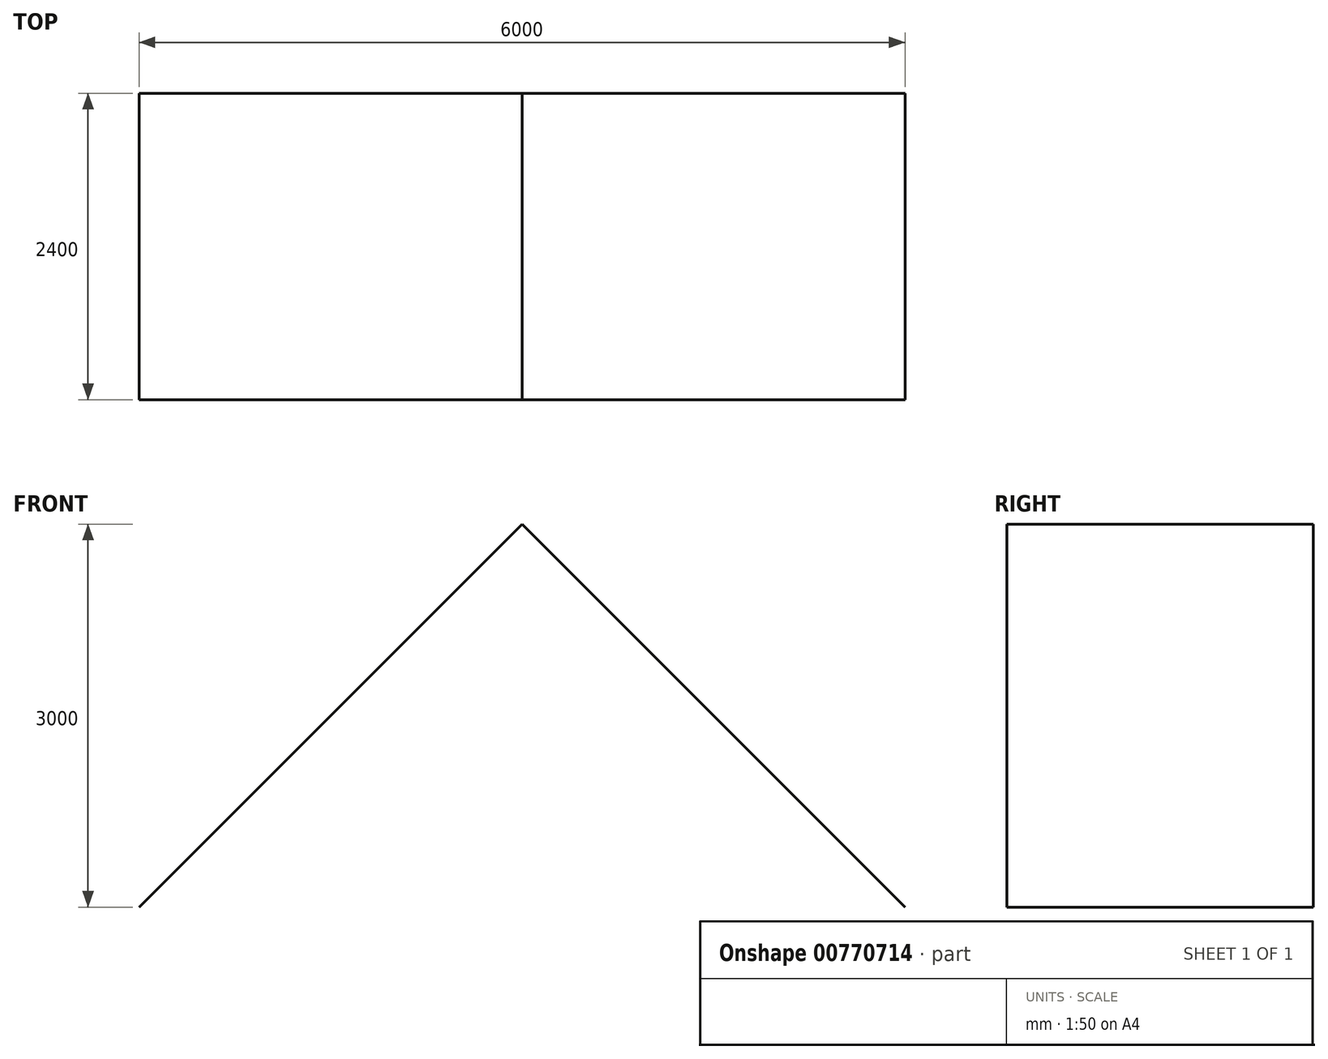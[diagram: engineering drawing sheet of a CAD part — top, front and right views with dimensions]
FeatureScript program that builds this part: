
annotation { "Feature Type Name" : "Feature", "Feature Type Description" : "" }
export const myFeature = defineFeature(function(context is Context, id is Id, definition is map)
    precondition{}
    {
        {
            var Q0;
            Q0=qCreatedBy(makeId("Front.planeOp"),FACE);
            var sketch = newSketch(context, id + "F0", { "sketchPlane" : qUnion([Q0])});
            skLineSegment(sketch, "E0", {"start": v(-3000, 0) * mm, "end": v(0, 3000) * mm});
            skLineSegment(sketch, "E1.MirrorCS", {"start": v(3000, 0) * mm, "end": v(0, 3000) * mm});
            skLineSegment(sketch, "E2", {"start": v(-3000, 0) * mm, "end": v(0, 0) * mm, "construction": true});
            skSolve(sketch);
        }
        {
            var Q0;
            Q0 = qSketchRegion(id + "F0", true);
            var Q1;
            Q1=sQuery(id+"F0.wireOp",EDGE,"E0");
            var Q2;
            Q2=sQuery(id+"F0.wireOp",EDGE,"E1.MirrorCS");
            extrude(context, id + "F1", {"entities" : qUnion([Q0]), "bodyType" : ToolBodyType.SURFACE, "surfaceEntities" : qUnion([Q1, Q2]), "depth" : 2400 * mm, "offsetDistance" : 25 * mm});
        }
    });
